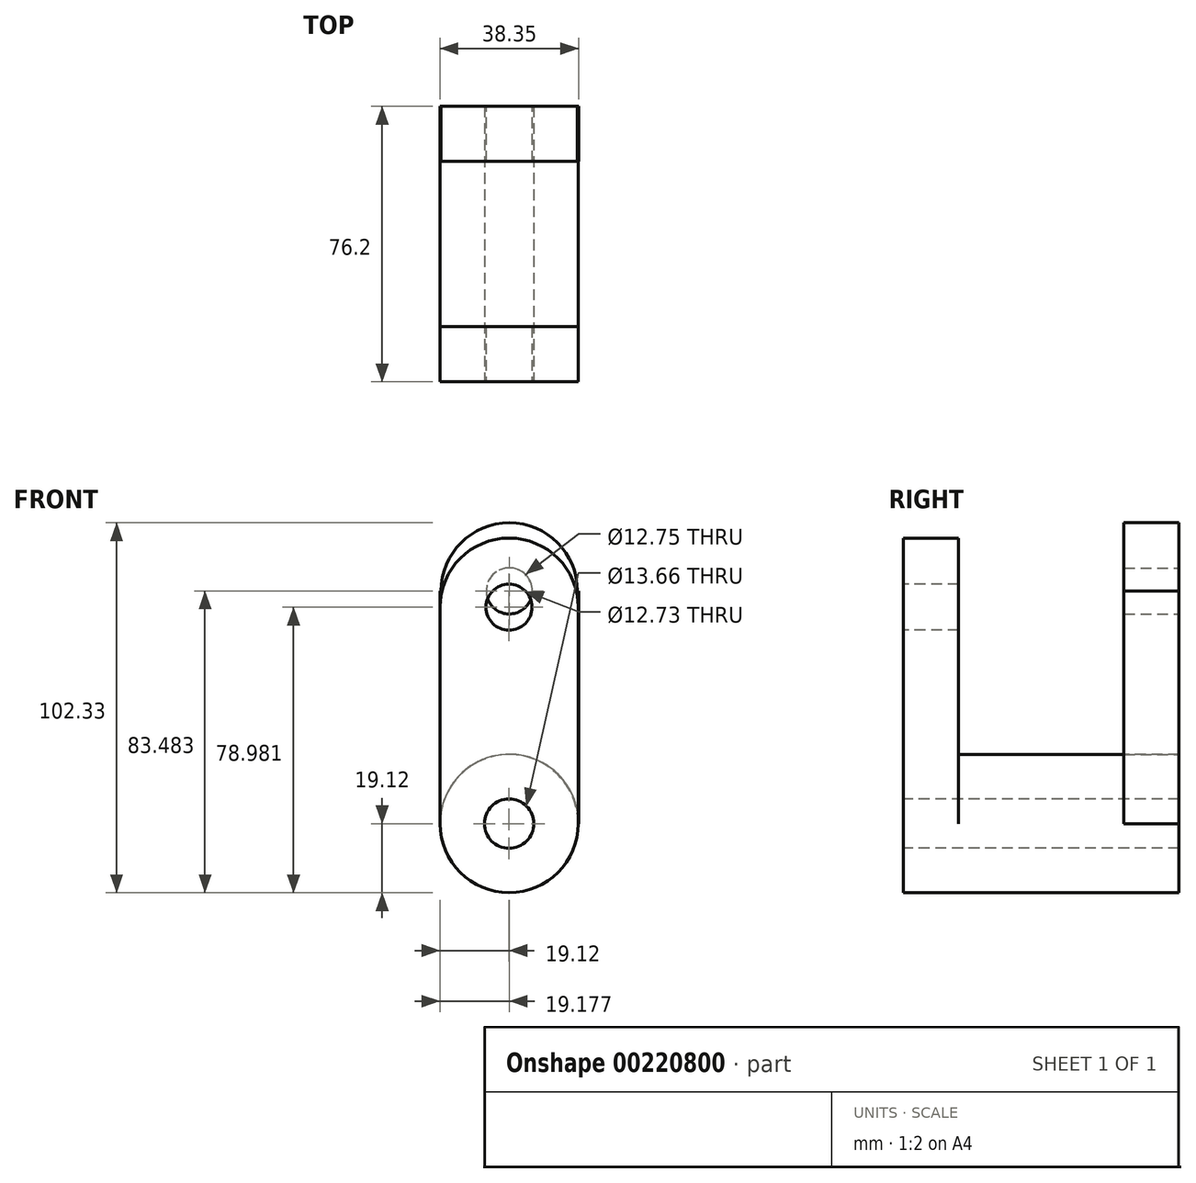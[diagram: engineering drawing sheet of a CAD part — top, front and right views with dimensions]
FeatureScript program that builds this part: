
annotation { "Feature Type Name" : "Feature", "Feature Type Description" : "" }
export const myFeature = defineFeature(function(context is Context, id is Id, definition is map)
    precondition{}
    {
        {
            var Q0;
            Q0=qCreatedBy(makeId("Front.planeOp"),FACE);
            var sketch = newSketch(context, id + "F0", { "sketchPlane" : qUnion([Q0])});
            skCircle(sketch, "E0", {"center": v(0, 0) * mm, "radius": 19.12 * mm});
            skCircle(sketch, "E1", {"center": v(0, 0) * mm, "radius": 6.83 * mm});
            skSolve(sketch);
        }
        {
            var Q0;
            Q0=makeQuery(id+"F0.imprint","IMPRINT",FACE,{"disambiguationData":[TD([[makeQuery(id+"F0.imprint","IMPRINT",EDGE,{"derivedFrom":sQuery(id+"F0.wireOp",EDGE,"E0")}),1.0]])]});
            extrude(context, id + "F1", {"entities" : qUnion([Q0]), "oppositeDirection" : true, "depth" : 76.2 * mm});
        }
        {
            var Q0;
            Q0=qCreatedBy(makeId("Front.planeOp"),FACE);
            var sketch = newSketch(context, id + "F2", { "sketchPlane" : qUnion([Q0])});
            skLineSegment(sketch, "E2.top", {"start": v(-19.12, 59.86) * mm, "end": v(19.12, 59.86) * mm});
            skLineSegment(sketch, "E2.left", {"start": v(-19.12, 0) * mm, "end": v(-19.12, 59.86) * mm});
            skLineSegment(sketch, "E2.right", {"start": v(19.12, 0) * mm, "end": v(19.12, 59.86) * mm});
            skCircle(sketch, "E3", {"center": v(0, 59.86) * mm, "radius": 19.12 * mm});
            skCircle(sketch, "E4", {"center": v(0, 59.86) * mm, "radius": 6.36 * mm});
            skArc(sketch, "E5", {"start": v(19.12, 0) * mm, "mid": v(0, 19.12) * mm, "end": v(-19.12, 0) * mm});
            skSolve(sketch);
        }
        {
            var Q0;
            Q0 = qSketchRegion(id + "F2", true);
            extrude(context, id + "F3", {"entities" : qUnion([Q0]), "operationType" : NewBodyOperationType.ADD, "oppositeDirection" : true, "depth" : 15.24 * mm});
        }
        {
            var Q0;
            Q0=makeQuery(id+"F1.opExtrude","CAP_FACE",FACE,{"disambiguationData":[OSD([sQuery(id+"F0.wireOp",EDGE,"E0"),sQuery(id+"F0.wireOp",EDGE,"E1")])],"isStart":false});
            var sketch = newSketch(context, id + "F4", { "sketchPlane" : qUnion([Q0])});
            skLineSegment(sketch, "E6.top", {"start": v(19.12, 64.36) * mm, "end": v(-19.23, 64.36) * mm});
            skLineSegment(sketch, "E6.left", {"start": v(19.12, 0) * mm, "end": v(19.12, 64.36) * mm});
            skLineSegment(sketch, "E6.right", {"start": v(-19.23, 0) * mm, "end": v(-19.23, 64.36) * mm});
            skCircle(sketch, "E7", {"center": v(-0.06, 64.36) * mm, "radius": 18.85 * mm});
            skCircle(sketch, "E8", {"center": v(-0.06, 64.36) * mm, "radius": 6.38 * mm});
            skArc(sketch, "E9", {"start": v(19.12, 0) * mm, "mid": v(-0.06, 19.17) * mm, "end": v(-19.23, 0) * mm});
            skSolve(sketch);
        }
        {
            var Q0;
            Q0 = qSketchRegion(id + "F4", true);
            extrude(context, id + "F5", {"entities" : qUnion([Q0]), "oppositeDirection" : true, "depth" : 15.24 * mm});
        }
    });
